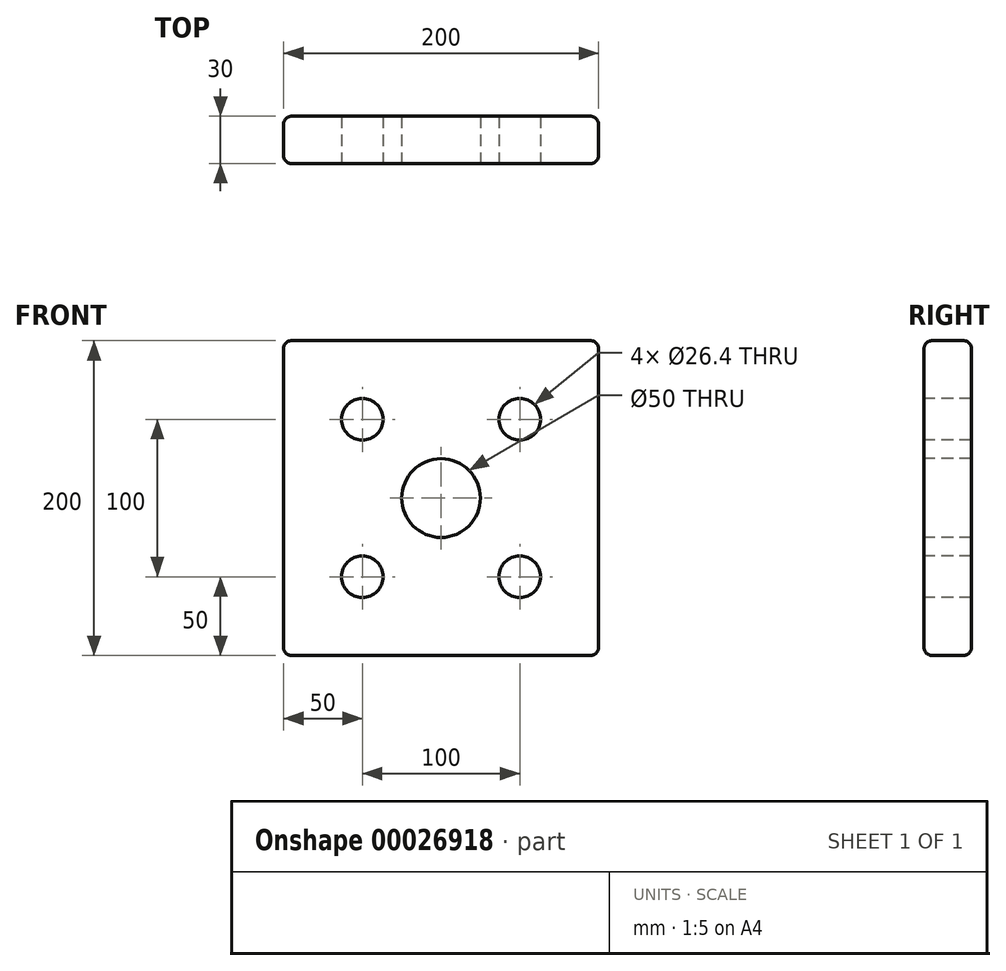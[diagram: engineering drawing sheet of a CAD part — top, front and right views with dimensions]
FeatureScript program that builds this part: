
annotation { "Feature Type Name" : "Feature", "Feature Type Description" : "" }
export const myFeature = defineFeature(function(context is Context, id is Id, definition is map)
    precondition{}
    {
        {
            var Q0;
            Q0=qCreatedBy(makeId("Front.planeOp"),FACE);
            var sketch = newSketch(context, id + "F0", { "sketchPlane" : qUnion([Q0])});
            skLineSegment(sketch, "E0.bottom", {"start": v(-100, 100) * mm, "end": v(100, 100) * mm});
            skLineSegment(sketch, "E0.top", {"start": v(-100, -100) * mm, "end": v(100, -100) * mm});
            skLineSegment(sketch, "E0.left", {"start": v(-100, 100) * mm, "end": v(-100, -100) * mm});
            skLineSegment(sketch, "E0.right", {"start": v(100, 100) * mm, "end": v(100, -100) * mm});
            skSolve(sketch);
        }
        {
            var Q0;
            Q0=qSketchRegion(id+"F0",true);
            extrude(context, id + "F1", {"entities" : qUnion([Q0]), "depth" : 30 * mm});
        }
        {
            var Q0;
            Q0=makeQuery(id+"F1.opExtrude","CAP_FACE",FACE,{"disambiguationData":[OSD([sQuery(id+"F0.wireOp",EDGE,"E0.bottom"),sQuery(id+"F0.wireOp",EDGE,"E0.top"),sQuery(id+"F0.wireOp",EDGE,"E0.left"),sQuery(id+"F0.wireOp",EDGE,"E0.right")])],"isStart":false});
            var sketch = newSketch(context, id + "F2", { "sketchPlane" : qUnion([Q0])});
            skCircle(sketch, "E1", {"center": v(0, 0) * mm, "radius": 25 * mm});
            skSolve(sketch);
        }
        {
            var Q0;
            Q0=makeQuery(id+"F1.opExtrude","CAP_FACE",FACE,{"disambiguationData":[OSD([sQuery(id+"F0.wireOp",EDGE,"E0.bottom"),sQuery(id+"F0.wireOp",EDGE,"E0.top"),sQuery(id+"F0.wireOp",EDGE,"E0.left"),sQuery(id+"F0.wireOp",EDGE,"E0.right")])],"isStart":false});
            var sketch = newSketch(context, id + "F3", { "sketchPlane" : qUnion([Q0])});
            skCircle(sketch, "E2", {"center": v(-50, -50) * mm, "radius": 13.2 * mm});
            skCircle(sketch, "E3.0.1.0", {"center": v(-50, 50) * mm, "radius": 13.2 * mm});
            skCircle(sketch, "E3.1.0.0", {"center": v(50, -50) * mm, "radius": 13.2 * mm});
            skCircle(sketch, "E3.1.1.0", {"center": v(50, 50) * mm, "radius": 13.2 * mm});
            skLineSegment(sketch, "E3.direction1", {"start": v(-50, -50) * mm, "end": v(50, -50) * mm, "construction": true});
            skLineSegment(sketch, "E3.direction2", {"start": v(-50, -50) * mm, "end": v(-50, 50) * mm, "construction": true});
            skLineSegment(sketch, "E4", {"start": v(-66.92, 0) * mm, "end": v(60.8, 0) * mm});
            skLineSegment(sketch, "E5", {"start": v(0, -49.75) * mm, "end": v(0, 68.34) * mm});
            skSolve(sketch);
        }
        {
            var Q0;
            Q0=makeQuery(id+"F1.opExtrude","SWEPT_FACE",FACE,{"disambiguationData":[OSD([sQuery(id+"F0.wireOp",EDGE,"E0.right")])]});
            var Q1;
            Q1=makeQuery(id+"F1.opExtrude","SWEPT_FACE",FACE,{"disambiguationData":[OSD([sQuery(id+"F0.wireOp",EDGE,"E0.top")])]});
            var Q2;
            Q2=makeQuery(id+"F1.opExtrude","CAP_EDGE",EDGE,{"disambiguationData":[OSD([sQuery(id+"F0.wireOp",EDGE,"E0.top")])],"isStart":true});
            var Q3;
            Q3=makeQuery(id+"F1.opExtrude","SWEPT_FACE",FACE,{"disambiguationData":[OSD([sQuery(id+"F0.wireOp",EDGE,"E0.left")])]});
            var Q4;
            Q4=makeQuery(id+"F1.opExtrude","SWEPT_FACE",FACE,{"disambiguationData":[OSD([sQuery(id+"F0.wireOp",EDGE,"E0.bottom")])]});
            fillet(context, id + "F4", {"entities" : qUnion([Q0, Q1, Q2, Q3, Q4]), "radius" : 5 * mm, "tangentPropagation" : true, "allowEdgeOverflow" : false});
        }
        {
            var Q0;
            Q0 = qSketchRegion(id + "F2", true);
            extrude(context, id + "F5", {"entities" : qUnion([Q0]), "operationType" : NewBodyOperationType.REMOVE, "endBound" : BoundingType.THROUGH_ALL, "oppositeDirection" : true, "depth" : 25 * mm});
        }
        {
            var Q0;
            Q0 = qSketchRegion(id + "F3", true);
            extrude(context, id + "F6", {"entities" : qUnion([Q0]), "operationType" : NewBodyOperationType.REMOVE, "endBound" : BoundingType.THROUGH_ALL, "oppositeDirection" : true, "depth" : 25 * mm});
        }
    });
